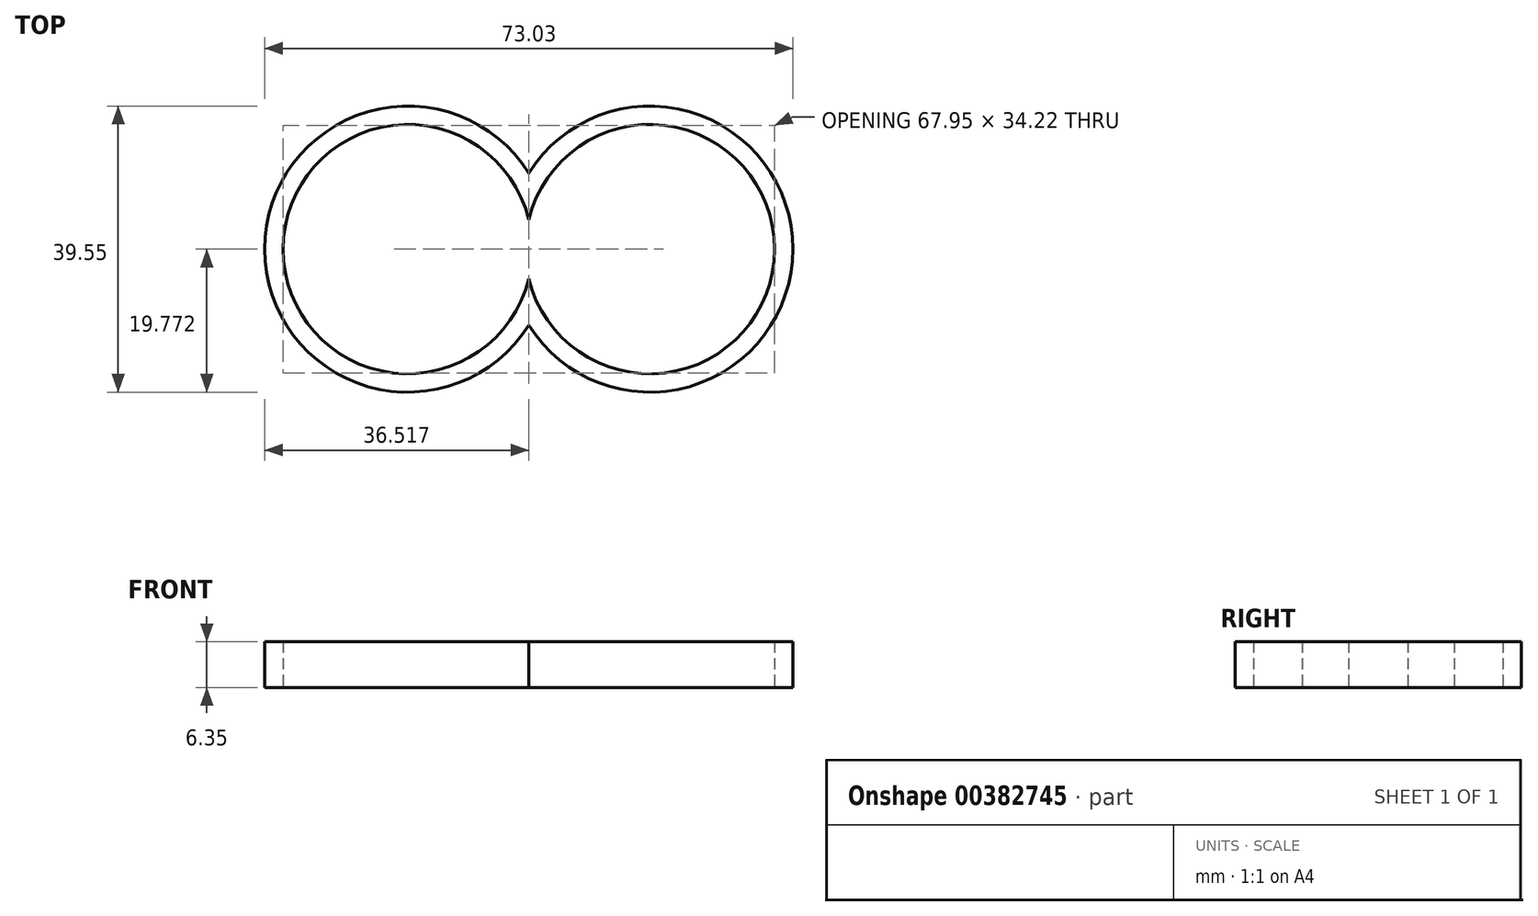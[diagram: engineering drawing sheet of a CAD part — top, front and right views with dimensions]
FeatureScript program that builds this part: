
annotation { "Feature Type Name" : "Feature", "Feature Type Description" : "" }
export const myFeature = defineFeature(function(context is Context, id is Id, definition is map)
    precondition{}
    {
        {
            var Q0;
            Q0=qCreatedBy(makeId("Top.planeOp"),FACE);
            var sketch = newSketch(context, id + "F0", { "sketchPlane" : qUnion([Q0])});
            skArc(sketch, "E0", {"start": v(-36.1, 38.52) * mm, "mid": v(-2.13, 42.62) * mm, "end": v(-36.1, 46.72) * mm});
            skArc(sketch, "E1", {"start": v(-36.1, 46.72) * mm, "mid": v(-70.08, 42.62) * mm, "end": v(-36.1, 38.52) * mm});
            skArc(sketch, "E2.0", {"start": v(-36.1, 53.15) * mm, "mid": v(-72.62, 42.62) * mm, "end": v(-36.1, 32.1) * mm});
            skArc(sketch, "E2.1", {"start": v(-36.1, 32.1) * mm, "mid": v(0.4, 42.62) * mm, "end": v(-36.1, 53.15) * mm});
            skSolve(sketch);
        }
        {
            var Q0;
            Q0 = qSketchRegion(id + "F0", true);
            extrude(context, id + "F1", {"entities" : qUnion([Q0]), "depth" : 6.35 * mm});
        }
    });
